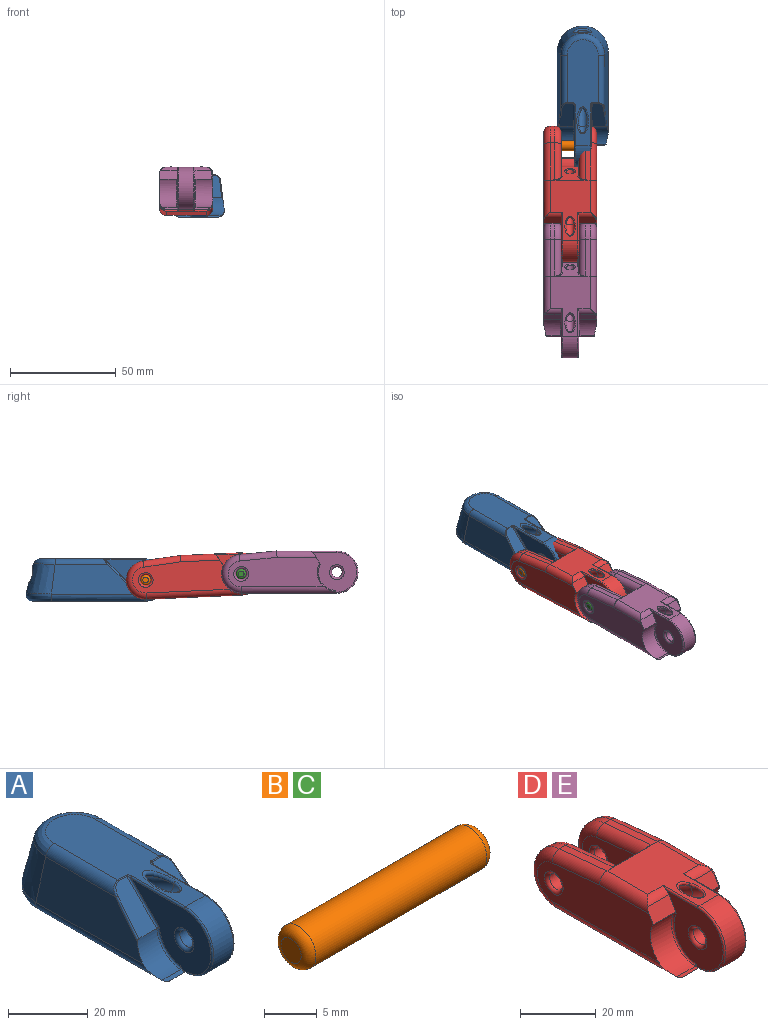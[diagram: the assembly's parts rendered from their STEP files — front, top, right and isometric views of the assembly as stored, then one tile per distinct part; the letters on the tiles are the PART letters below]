
ASSEMBLY  parts=5 mates=4
PART A: 48 faces, bbox 25.4x68.7x23 mm
  f0: bspline ~57.5x25mm, area 444.8mm2, adj f7,f8,f16,f19,f46
  f1: plane 8x1.73mm, normal (0,-0.71,0.71), area 7.3mm2, adj f5,f12,f14,f18,f23,f24
  f2: plane 10.64x10.64mm, normal (0,-0.71,0.71), area 84.7mm2, adj f13,f33,f36,f37,f38
  f3: plane 8x1.73mm, normal (0,-0.71,0.71), area 7.3mm2, adj f5,f11,f13,f20,f31,f32
  f4: plane 10.64x10.64mm, normal (0,-0.71,0.71), area 84.7mm2, adj f14,f26,f28,f29,f30
  f5: plane 53.66x18.2mm, normal (0,0,-1), area 941.2mm2, adj f1,f3,f9,f18,f19,f20
  f6: plane 50.16x14.7mm, normal (0,0,1), area 503.8mm2, adj f9,f15,f16,f17,f25,f27,f28,f34
  f7: plane 38.18x14.05mm, normal (0.99,0,0.12), area 453.1mm2, adj f0,f13,f17,f20,f38
  f8: plane 38.18x14.05mm, normal (-0.99,0,0.12), area 453.1mm2, adj f0,f14,f15,f18,f30
  f9: cylinder r=10mm len=20mm, axis (-1,0,0), area 219.9mm2, adj f5,f6,f23,f32
  f10: cylinder r=2.5mm len=6mm, axis (-1,0,0), area 94.2mm2, adj f21,f22
  f11: plane 28.29x19mm, normal (1,0,0), area 297.7mm2, adj f3,f22,f31,f32,f33,f34
  f12: plane 28.29x19mm, normal (-1,0,0), area 297.7mm2, adj f1,f21,f23,f24,f25,f26
  f13: cylinder r=9.25mm len=8.43mm, axis (-1,0,0), area 92.6mm2, adj f2,f3,f7,f20,f31,f38
  f14: cylinder r=9.25mm len=8.43mm, axis (1,0,0), area 92.6mm2, adj f1,f4,f8,f18,f24,f30
  f15: cylinder r=3mm len=24.81mm, axis (0,1,0), area 102.9mm2, adj f6,f8,f16,f29
  f16: bspline ~20.66x10.42mm, area 117.4mm2, adj f0,f6,f15,f17
  f17: cylinder r=3mm len=24.81mm, axis (0,1,0), area 102.9mm2, adj f6,f7,f16,f37
  f18: cylinder r=3mm len=44.58mm, axis (0,-1,0), area 215.5mm2, adj f1,f5,f8,f14,f19
  f19: bspline ~25.02x13.09mm, area 185.8mm2, adj f0,f5,f18,f20
  f20: cylinder r=3mm len=44.58mm, axis (0,-1,0), area 215.5mm2, adj f3,f5,f7,f13,f19
  f21: torus R=3.5mm, axis (1,0,0), area 28.3mm2, adj f10,f12
  f22: torus R=3.5mm, axis (1,0,0), area 28.3mm2, adj f10,f11
  f23: torus R=9.5mm, axis (1,0,0), area 24.4mm2, adj f1,f9,f12,f25
  f24: torus R=8.75mm, axis (1,0,0), area 9.8mm2, adj f1,f12,f14,f26
  f25: cylinder r=0.5mm len=18.79mm, axis (0,-1,0), area 14.8mm2, adj f6,f12,f23,f27
  f26: cylinder r=0.5mm len=11.12mm, axis (0,0.71,0.71), area 11.5mm2, adj f4,f12,f24,f27
  f27: bspline ~1.66x1mm, area 0.9mm2, adj f6,f25,f26,f28
  f28: cylinder r=0.5mm len=2.85mm, axis (1,0,0), area 1.1mm2, adj f4,f6,f27,f29
  f29: bspline ~2.98x2.63mm, area 2.5mm2, adj f4,f15,f28,f30
  f30: cylinder r=0.5mm len=9.25mm, axis (-0.09,-0.7,-0.7), area 9.1mm2, adj f4,f8,f14,f29
  f31: torus R=8.75mm, axis (1,0,0), area 9.8mm2, adj f3,f11,f13,f33
  f32: torus R=9.5mm, axis (1,0,0), area 24.4mm2, adj f3,f9,f11,f34
  f33: cylinder r=0.5mm len=11.12mm, axis (0,-0.71,-0.71), area 11.5mm2, adj f2,f11,f31,f35
  f34: cylinder r=0.5mm len=18.79mm, axis (0,1,0), area 14.8mm2, adj f6,f11,f32,f35
  f35: bspline ~1.66x1.17mm, area 0.9mm2, adj f6,f33,f34,f36
  f36: cylinder r=0.5mm len=2.85mm, axis (1,0,0), area 1.1mm2, adj f2,f6,f35,f37
  f37: bspline ~2.98x2.63mm, area 2.5mm2, adj f2,f17,f36,f38
  f38: cylinder r=0.5mm len=9.25mm, axis (-0.09,0.7,0.7), area 9.1mm2, adj f2,f7,f13,f37
  f39: cylinder r=2mm len=5mm, axis (0,-1,0), area 62.8mm2, adj f40,f42
  f40: torus R=66.02mm, axis (-1,0,0), area 377mm2, adj f39,f41,f45
  f41: cylinder r=2mm len=3.78mm, axis (0,-0.88,0.48), area 11.2mm2, adj f40,f44
  f42: plane 4.9x4.9mm, normal (0,1,0), area 6.3mm2, adj f39,f47
  f43: cylinder r=3.25mm len=7.39mm, axis (0,1,0), area 121.7mm2, adj f46,f47
  f44: bspline ~5.3x4.08mm, area 6.6mm2, adj f6,f41,f45
  f45: bspline ~9.51x5.61mm, area 27.9mm2, adj f6,f40,f44
  f46: bspline ~8.73x8.11mm, area 32.9mm2, adj f0,f43
  f47: torus R=2.45mm, axis (0,-1,0), area 23.4mm2, adj f42,f43
PART B: 5 faces, bbox 25x5.1x5.1 mm
  f0: cylinder r=2.35mm len=23mm, axis (-1,0,0), area 339.6mm2, adj f3,f4
  f1: plane 2.7x2.7mm, normal (1,0,0), area 5.7mm2, adj f4
  f2: plane 2.7x2.7mm, normal (-1,0,0), area 5.7mm2, adj f3
  f3: torus R=1.35mm, axis (1,0,0), area 19.6mm2, adj f0,f2
  f4: torus R=1.35mm, axis (1,0,0), area 19.6mm2, adj f0,f1
PART C: same geometry as B
PART D: 66 faces, bbox 25.7x66.7x24.1 mm
  f0: plane 14.55x0.99mm, normal (0,0.87,0.5), area 10.3mm2, adj f5,f24,f35,f38
  f1: plane 11.95x11.62mm, normal (0,0.87,0.5), area 80.8mm2, adj f6,f24,f50,f51,f52,f53,f65
  f2: plane 8.04x1.49mm, normal (0,-0.87,0.5), area 6mm2, adj f5,f12,f19,f26,f56,f58
  f3: plane 8.47x4.92mm, normal (0,-0.87,0.5), area 40.8mm2, adj f7,f13,f14,f30,f32,f59
  f4: plane 8.04x1.49mm, normal (0,-0.87,0.5), area 6mm2, adj f5,f13,f14,f31,f54,f59
  f5: plane 45.28x19mm, normal (0,0,-1), area 784.7mm2, adj f0,f2,f4,f10,f17,f20,f26,f31
  f6: plane 29.29x19.7mm, normal (0,0,1), area 349.4mm2, adj f1,f10,f15,f21,f25,f27,f30,f32
  f7: plane 45.39x14mm, normal (-1,0,0), area 520.1mm2, adj f3,f14,f31,f32,f33,f34,f43
  f8: plane 7.97x4.92mm, normal (0,-0.87,0.5), area 38.4mm2, adj f12,f19,f25,f47,f48,f58
  f9: plane 45.39x14mm, normal (1,0,0), area 518.4mm2, adj f19,f26,f27,f28,f29,f41,f47
  f10: cylinder r=10mm len=20mm, axis (-1,0,0), area 230.4mm2, adj f5,f6,f54,f56
  f11: cylinder r=2.5mm len=6.33mm, axis (-1,0,0), area 99.5mm2, adj f45,f46
  f12: plane 21.12x19mm, normal (1,0,0), area 250.9mm2, adj f2,f8,f25,f46,f56,f57,f58
  f13: plane 21.12x19mm, normal (-1,0,0), area 250.9mm2, adj f3,f4,f30,f45,f54,f55,f59
  f14: cylinder r=9.25mm len=13.48mm, axis (1,0,0), area 141.8mm2, adj f3,f4,f7,f31,f59
  f15: plane 17.79x2.39mm, normal (0,0.1,1), area 41.5mm2, adj f6,f17,f34,f40,f51
  f16: cylinder r=2.5mm len=6.33mm, axis (-1,0,0), area 99.5mm2, adj f43,f44
  f17: cylinder r=9.15mm len=18.26mm, axis (-1,0,0), area 65mm2, adj f5,f15,f33,f39
  f18: plane 20.52x13.74mm, normal (1,0,0), area 161.6mm2, adj f24,f38,f39,f40,f44,f50
  f19: cylinder r=9.25mm len=13.48mm, axis (-1,0,0), area 141.6mm2, adj f2,f8,f9,f26,f47,f58
  f20: cylinder r=9.15mm len=18.26mm, axis (1,0,0), area 65mm2, adj f5,f21,f28,f36
  f21: plane 17.79x2.39mm, normal (0,0.1,1), area 41.5mm2, adj f6,f20,f29,f37,f53
  f22: cylinder r=2.5mm len=6.33mm, axis (1,0,0), area 99.5mm2, adj f41,f42
  f23: plane 20.52x13.74mm, normal (-1,0,0), area 161.6mm2, adj f24,f35,f36,f37,f42,f52
  f24: cylinder r=10.15mm len=10.32mm, axis (-1,0,0), area 79.5mm2, adj f0,f1,f18,f23,f35,f38,f50,f52
  f25: cylinder r=3mm len=8mm, axis (-1,0,0), area 20.6mm2, adj f6,f8,f12,f49,f57
  f26: cylinder r=3mm len=45.28mm, axis (0,1,0), area 204.7mm2, adj f2,f5,f9,f19,f28
  f27: cylinder r=3mm len=18.06mm, axis (0,-1,0), area 78.5mm2, adj f6,f9,f29,f48,f49
  f28: torus R=6.15mm, axis (-1,0,0), area 115.6mm2, adj f9,f20,f26,f29
  f29: cylinder r=3mm len=18.02mm, axis (0,1,-0.1), area 83.6mm2, adj f9,f21,f27,f28
  f30: cylinder r=3mm len=8.43mm, axis (-1,0,0), area 21.3mm2, adj f3,f6,f13,f32,f55
  f31: cylinder r=3mm len=45.28mm, axis (0,1,0), area 204.7mm2, adj f4,f5,f7,f14,f33
  f32: cylinder r=3mm len=18.64mm, axis (0,-1,0), area 80mm2, adj f3,f6,f7,f30,f34
  f33: torus R=6.15mm, axis (-1,0,0), area 115.6mm2, adj f7,f17,f31,f34
  f34: cylinder r=3mm len=18.02mm, axis (0,1,-0.1), area 83.6mm2, adj f7,f15,f32,f33
  f35: cylinder r=3mm len=8.07mm, axis (0,1,0), area 29.5mm2, adj f0,f5,f23,f24,f36
  f36: torus R=6.15mm, axis (1,0,0), area 115.6mm2, adj f20,f23,f35,f37
  f37: cylinder r=3mm len=17.76mm, axis (0,1,-0.1), area 76.8mm2, adj f21,f23,f36,f53
  f38: cylinder r=3mm len=8.07mm, axis (0,1,0), area 29.5mm2, adj f0,f5,f18,f24,f39
  f39: torus R=6.15mm, axis (-1,0,0), area 115.6mm2, adj f17,f18,f38,f40
  f40: cylinder r=3mm len=17.76mm, axis (0,-1,0.1), area 76.8mm2, adj f15,f18,f39,f51
  f41: torus R=3.5mm, axis (-1,0,0), area 28.3mm2, adj f9,f22
  f42: torus R=3.5mm, axis (1,0,0), area 28.3mm2, adj f22,f23
  f43: torus R=3.5mm, axis (-1,0,0), area 28.3mm2, adj f7,f16
  f44: torus R=3.5mm, axis (-1,0,0), area 28.3mm2, adj f16,f18
  f45: torus R=3.5mm, axis (1,0,0), area 28.3mm2, adj f11,f13
  f46: torus R=3.5mm, axis (1,0,0), area 28.3mm2, adj f11,f12
  f47: cylinder r=0.5mm len=3.56mm, axis (0,0.5,0.87), area 2.9mm2, adj f8,f9,f19,f48
  f48: bspline ~1.56x1.15mm, area 1.2mm2, adj f8,f27,f47,f49
  f49: bspline ~2.69x2.69mm, area 0.9mm2, adj f25,f27,f48
  f50: cylinder r=0.5mm len=8.36mm, axis (0,-0.5,0.87), area 7mm2, adj f1,f18,f24,f51
  f51: bspline ~4.69x3.73mm, area 3.7mm2, adj f1,f6,f15,f40,f50
  f52: cylinder r=0.5mm len=8.36mm, axis (0,-0.5,0.87), area 7mm2, adj f1,f23,f24,f53
  f53: bspline ~4.69x3.73mm, area 3.7mm2, adj f1,f6,f21,f37,f52
  f54: torus R=9.5mm, axis (1,0,0), area 24.3mm2, adj f4,f10,f13,f55
  f55: cylinder r=0.5mm len=13.28mm, axis (0,-1,0), area 9.8mm2, adj f6,f13,f30,f54
  f56: torus R=9.5mm, axis (1,0,0), area 24.3mm2, adj f2,f10,f12,f57
  f57: cylinder r=0.5mm len=13.28mm, axis (0,1,0), area 9.8mm2, adj f6,f12,f25,f56
  f58: torus R=8.75mm, axis (1,0,0), area 14mm2, adj f2,f8,f12,f19
  f59: torus R=8.75mm, axis (1,0,0), area 14mm2, adj f3,f4,f13,f14
  f60: cylinder r=2mm len=4mm, axis (0,-1,0), area 31.3mm2, adj f61,f65
  f61: torus R=40mm, axis (-1,0,0), area 281.9mm2, adj f60,f62,f64
  f62: cylinder r=2mm len=6.83mm, axis (0,-0.84,0.54), area 31.9mm2, adj f61,f63
  f63: bspline ~7.23x5mm, area 10.2mm2, adj f6,f62,f64
  f64: bspline ~4.6x3.04mm, area 6.4mm2, adj f6,f61,f63
  f65: bspline ~5x5mm, area 11.7mm2, adj f1,f60
PART E: same geometry as D
PLACE A t=(35.11,7.31,-19.58)mm
PLACE B t=(29.16,7.31,-19.58)mm
PLACE C t=(29.16,-37.89,-16.71)mm
PLACE D rot(axis=(-1,0,0),2.6deg) t=(29.16,-40.85,-17.59)mm
PLACE E t=(29.16,-85.67,-15.86)mm
MATE revolute E.f43 <-> C.f0  axis (1,0,0) through (41.66,-60.39,-6.71)mm
MATE cylindrical A.f9 <-> B.f0  axis (-1,0,0) through (38.11,-15.19,-9.58)mm
MATE revolute B.f0 <-> D.f43  axis (1,0,0) through (41.66,-15.19,-9.58)mm
MATE cylindrical D.f10 <-> C.f0  axis (-1,0,0) through (29.16,-60.39,-6.71)mm
